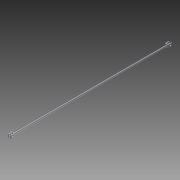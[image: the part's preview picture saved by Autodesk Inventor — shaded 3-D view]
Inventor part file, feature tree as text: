
AUTODESK INVENTOR PART (.ipt)
format: ipt  version: 2012 (Build 160160000, 160)  size: 126,976 bytes
history: native  units: in
note: dims shown in document units (in); Inventor stores cm internally (conversion verified against a paired STEP export)
features: extrude x3, sketch x3, projected_geometry x2, fillet x1
ambient origin geometry x8: Origin, YZ Plane, XZ Plane, XY Plane, X Axis, Y Axis, Z Axis, Center Point
bodies: Solid1 (feature_tree)
feature tree (9):
  extrude  "Extrusion1"  Depth=0.5in
  extrude  "Extrusion2"  Depth=0.625in
  extrude  "Extrusion3"  Depth=0.625in
  fillet  "Fillet1"  Radius=0.5in
  sketch  "Sketch1"  dims[d0=0.5in d1=0.5in]
  sketch  "Sketch2"  dims[d2=25.5312in d3=0.0in d4=0.625in]
  sketch  "Sketch3"  dims[d5=0.25in d6=0.625in d7=0.5in d8=0.5in d9=25.0in d10=0.0in d11=0.25in d12=0.25in d13=0.25in d14=0.25in d15=0.125in d16=0.25in d17=0.25in d18=0.25in d19=25.0in d20=0.0in d21=0.125in]
  projected_geometry  "Projected Loop1"
  projected_geometry  "Projected Loop2"
